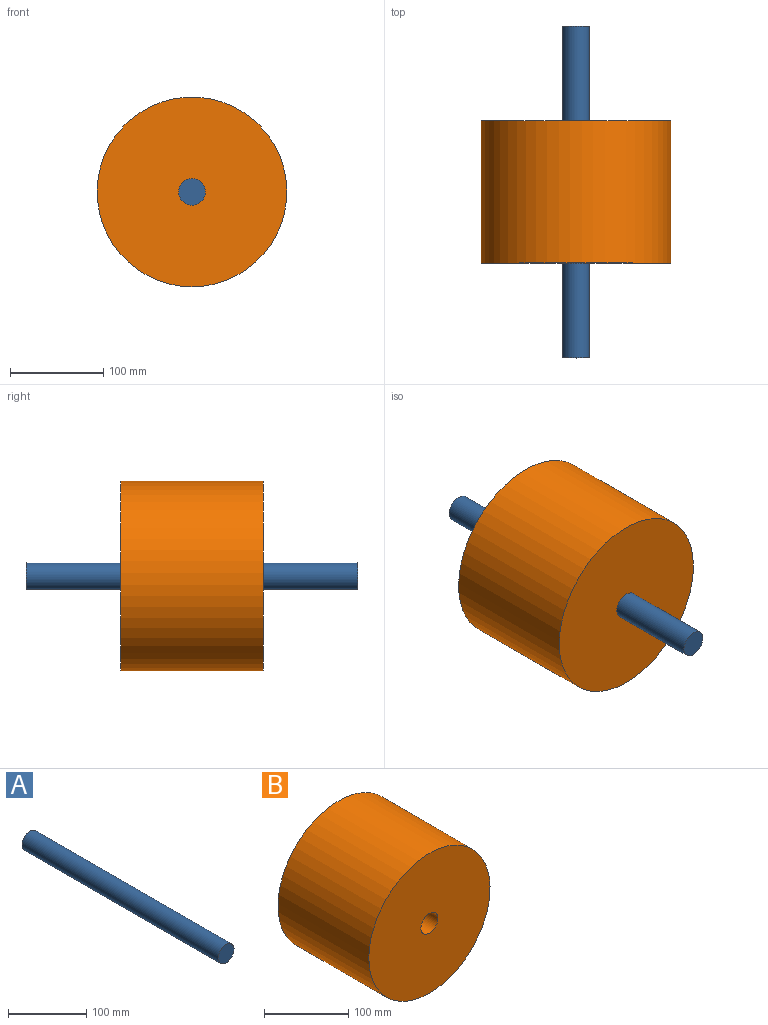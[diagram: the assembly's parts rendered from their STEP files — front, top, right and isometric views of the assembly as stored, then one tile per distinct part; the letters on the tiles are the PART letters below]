
ASSEMBLY  parts=2 mates=1
PART A: 3 faces, bbox 28.6x355.6x28.6 mm
  f0: cylinder r=14.29mm len=355.6mm, axis (0,1,0), area 31922.6mm2, adj f1,f2
  f1: plane 28.58x28.58mm, normal (0,-1,0), area 641.3mm2, adj f0
  f2: plane 28.58x28.58mm, normal (0,1,0), area 641.3mm2, adj f0
PART B: 4 faces, bbox 203.2x152.4x203.2 mm
  f0: cylinder r=101.6mm len=203.2mm, axis (0,-1,0), area 97287.8mm2, adj f1,f2
  f1: plane 203.2x203.2mm, normal (0,1,0), area 31788mm2, adj f0,f3
  f2: plane 203.2x203.2mm, normal (0,-1,0), area 31788mm2, adj f0,f3
  f3: cylinder r=14.29mm len=152.4mm, axis (0,-1,0), area 13681.1mm2, adj f1,f2
PLACE A t=(0,-76.2,-304.8)mm
PLACE B t=(0,-76.2,-304.8)mm
MATE fastened A.f0 <-> B.f0  axis (0,1,0) through (0,0,0)mm
